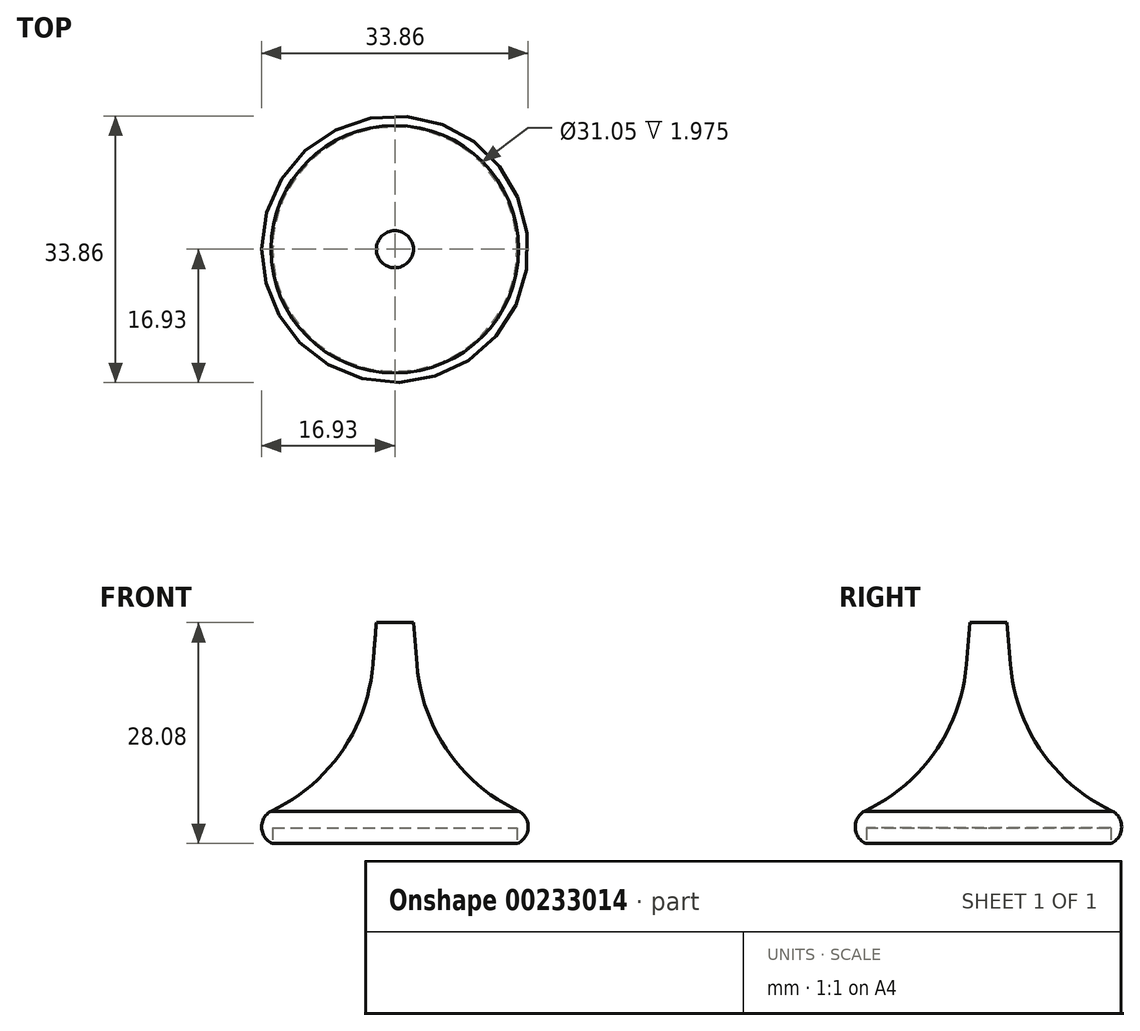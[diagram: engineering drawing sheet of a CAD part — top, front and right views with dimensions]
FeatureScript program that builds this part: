
annotation { "Feature Type Name" : "Feature", "Feature Type Description" : "" }
export const myFeature = defineFeature(function(context is Context, id is Id, definition is map)
    precondition{}
    {
        {
            var Q0;
            Q0=qCreatedBy(makeId("Front.planeOp"),FACE);
            var sketch = newSketch(context, id + "F0", { "sketchPlane" : qUnion([Q0])});
            skLineSegment(sketch, "E0", {"start": v(0, 0) * mm, "end": v(0, 63.32) * mm});
            skLineSegment(sketch, "E1", {"start": v(0, 0) * mm, "end": v(0, 25.48) * mm});
            skLineSegment(sketch, "E2", {"start": v(0, 25.48) * mm, "end": v(-25.33, 25.48) * mm});
            skArc(sketch, "E3", {"start": v(0, 0) * mm, "mid": v(-7.37, 18) * mm, "end": v(-25.33, 25.48) * mm});
            skPoint(sketch, "E4.second.point", {"position": v(-25.33, 63.32) * mm});
            skPoint(sketch, "E4.third.point", {"position": v(-42.02, 52.9) * mm});
            skArc(sketch, "E5", {"start": v(-25.33, 25.48) * mm, "mid": v(-10, 31.46) * mm, "end": v(-2.79, 46.24) * mm});
            skLineSegment(sketch, "E6", {"start": v(-2.79, 46.24) * mm, "end": v(-2.35, 51.58) * mm});
            skLineSegment(sketch, "E7", {"start": v(-2.35, 51.58) * mm, "end": v(0, 51.58) * mm});
            skLineSegment(sketch, "E8", {"start": v(-15.52, 31.12) * mm, "end": v(-15.52, 20.46) * mm});
            skArc(sketch, "E9", {"start": v(-15.52, 27.71) * mm, "mid": v(-16.93, 25.6) * mm, "end": v(-15.52, 23.5) * mm});
            skSolve(sketch);
        }
        {
            var Q0;
            {var subQ0=sQuery(id+"F0.wireOp",EDGE,"E6");Q0=makeQuery(id+"F0.imprint","IMPRINT",FACE,{"disambiguationData":[TD([[makeQuery(id+"F0.imprint","IMPRINT",EDGE,{"derivedFrom":subQ0}),-1.0]])]});}
            var Q1;
            {var subQ1=sQuery(id+"F0.wireOp",EDGE,"E1");var subQ3=sQuery(id+"F0.wireOp",EDGE,"E3");var subQ4=makeQuery(id+"F0.imprint","INTERSECT",VERTEX,{"disambiguationData":[OD(1.0)],"derivedFrom":[subQ1,subQ3]});Q1=makeQuery(id+"F0.imprint","IMPRINT",FACE,{"disambiguationData":[TD([[makeQuery(id+"F0.imprint","IMPRINT",EDGE,{"disambiguationData":[TD([[subQ4,-1.0]])],"derivedFrom":subQ1}),1.0]])]});}
            var Q2;
            {var subQ0=sQuery(id+"F0.wireOp",EDGE,"E8");var subQ1=sQuery(id+"F0.wireOp",EDGE,"E2");var subQ2=makeQuery(id+"F0.imprint","INTERSECT",VERTEX,{"derivedFrom":[subQ1,subQ0]});Q2=makeQuery(id+"F0.imprint","IMPRINT",FACE,{"disambiguationData":[TD([[makeQuery(id+"F0.imprint","IMPRINT",EDGE,{"disambiguationData":[TD([[subQ2,-1.0]])],"derivedFrom":subQ1}),-1.0]])]});}
            var Q3;
            {var subQ0=sQuery(id+"F0.wireOp",EDGE,"E8");var subQ1=sQuery(id+"F0.wireOp",EDGE,"E2");var subQ2=makeQuery(id+"F0.imprint","INTERSECT",VERTEX,{"derivedFrom":[subQ1,subQ0]});Q3=makeQuery(id+"F0.imprint","IMPRINT",FACE,{"disambiguationData":[TD([[makeQuery(id+"F0.imprint","IMPRINT",EDGE,{"disambiguationData":[TD([[subQ2,-1.0]])],"derivedFrom":subQ1}),1.0]])]});}
            var Q4;
            Q4=sQuery(id+"F0.wireOp",EDGE,"E0");
            revolve(context, id + "F1", {"entities" : qUnion([Q0, Q1, Q2, Q3]), "axis" : qUnion([Q4]), "revolveType" : RevolveType.FULL});
        }
    });
